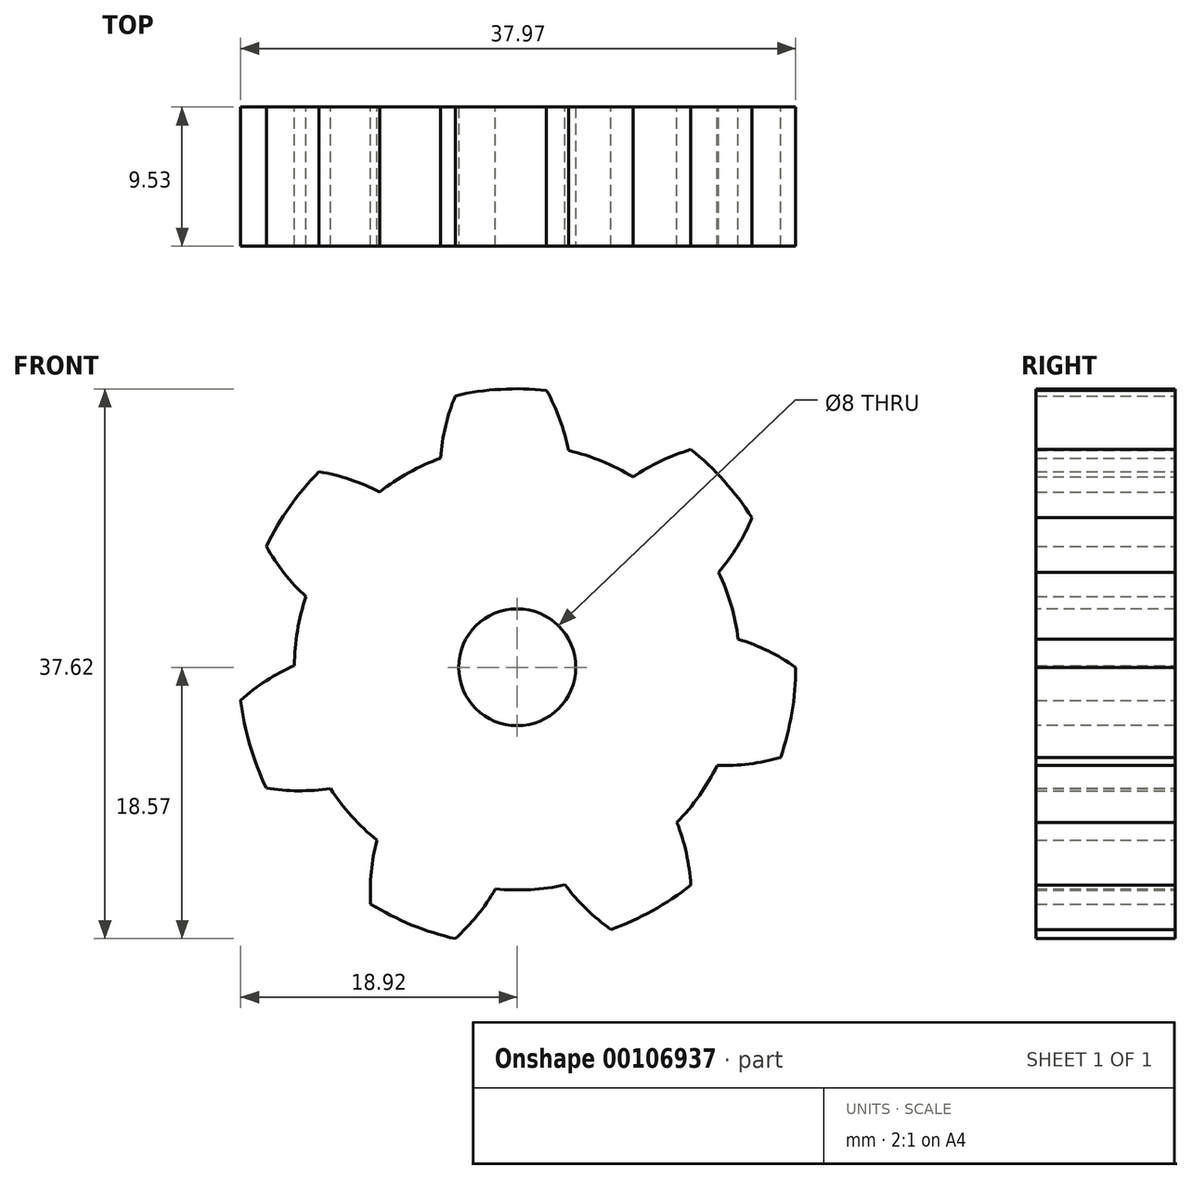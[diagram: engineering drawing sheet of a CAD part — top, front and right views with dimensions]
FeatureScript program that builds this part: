
annotation { "Feature Type Name" : "Feature", "Feature Type Description" : "" }
export const myFeature = defineFeature(function(context is Context, id is Id, definition is map)
    precondition{}
    {
        {
            var Q0;
            Q0=qCreatedBy(makeId("Front.planeOp"),FACE);
            var sketch = newSketch(context, id + "F0", { "sketchPlane" : qUnion([Q0])});
            skCircle(sketch, "E0", {"center": v(0, 0) * mm, "radius": 19.05 * mm, "construction": true});
            skCircle(sketch, "E1", {"center": v(0, 0) * mm, "radius": 15.88 * mm, "construction": true});
            skCircle(sketch, "E2", {"center": v(0, 0) * mm, "radius": 15.24 * mm, "construction": true});
            skLineSegment(sketch, "E3", {"start": v(0, 0) * mm, "end": v(0, 47.47) * mm, "construction": true});
            skLineSegment(sketch, "E4", {"start": v(0, 0) * mm, "end": v(-3.13, 52.63) * mm, "construction": true});
            skLineSegment(sketch, "E5", {"start": v(0, 15.88) * mm, "end": v(-34.16, 15.87) * mm, "construction": true});
            skLineSegment(sketch, "E6", {"start": v(0, 15.88) * mm, "end": v(-34.79, 3.21) * mm, "construction": true});
            skCircle(sketch, "E7", {"center": v(0, 15.88) * mm, "radius": 13.97 * mm, "construction": true});
            skCircle(sketch, "E8", {"center": v(-10.2, 12.16) * mm, "radius": 13.97 * mm, "construction": true});
            skArc(sketch, "E9", {"start": v(3.5, 14.83) * mm, "mid": v(2.92, 16.95) * mm, "end": v(2, 18.94) * mm});
            skArc(sketch, "E10.MirrorCS", {"start": v(-5.24, 14.31) * mm, "mid": v(-4.9, 16.48) * mm, "end": v(-4.24, 18.57) * mm});
            skArc(sketch, "E11", {"start": v(2, 18.94) * mm, "mid": v(-1.13, 19.02) * mm, "end": v(-4.24, 18.57) * mm});
            skArc(sketch, "E12", {"start": v(3.5, 14.83) * mm, "mid": v(-0.9, 15.21) * mm, "end": v(-5.24, 14.31) * mm});
            skSolve(sketch);
        }
        {
            var Q0;
            Q0=makeQuery(id+"F0.imprint","IMPRINT",FACE,{"disambiguationData":[TD([[makeQuery(id+"F0.imprint","IMPRINT",EDGE,{"derivedFrom":sQuery(id+"F0.wireOp",EDGE,"E9")}),1.0]])]});
            extrude(context, id + "F1", {"entities" : qUnion([Q0]), "depth" : 9.52 * mm});
        }
        {
            var Q0;
            Q0=makeQuery(id+"F1.opExtrude","SWEPT_BODY",BODY,{"disambiguationData":[OSD([sQuery(id+"F0.wireOp",EDGE,"E9"),sQuery(id+"F0.wireOp",EDGE,"E10.MirrorCS"),sQuery(id+"F0.wireOp",EDGE,"E11"),sQuery(id+"F0.wireOp",EDGE,"E12")])]});
            var Q1;
            Q1=sQuery(id+"F0.wireOp",EDGE,"E2");
            circularPattern(context, id + "F2", {"entities" : qUnion([Q0]), "axis" : qUnion([Q1]), "angle" : 360 * degree, "instanceCount" : 7, "equalSpace" : true});
        }
        {
            var Q0;
            Q0=qCreatedBy(makeId("Front.planeOp"),FACE);
            var sketch = newSketch(context, id + "F3", { "sketchPlane" : qUnion([Q0])});
            skCircle(sketch, "E13.0", {"center": v(0, 0) * mm, "radius": 15.24 * mm});
            skSolve(sketch);
        }
        {
            var Q0;
            Q0=makeQuery(id+"F3.imprint","IMPRINT",FACE,{"disambiguationData":[TD([[makeQuery(id+"F3.imprint","IMPRINT",EDGE,{"derivedFrom":sQuery(id+"F3.wireOp",EDGE,"E13.0")}),1.0]])]});
            var Q1;
            Q1=makeQuery(id+"F1.opExtrude","CAP_FACE",FACE,{"disambiguationData":[OSD([sQuery(id+"F0.wireOp",EDGE,"E9"),sQuery(id+"F0.wireOp",EDGE,"E10.MirrorCS"),sQuery(id+"F0.wireOp",EDGE,"E11"),sQuery(id+"F0.wireOp",EDGE,"E12")])],"isStart":false});
            extrude(context, id + "F4", {"entities" : qUnion([Q0]), "operationType" : NewBodyOperationType.ADD, "endBound" : BoundingType.UP_TO_SURFACE, "endBoundEntityFace" : qUnion([Q1]), "depth" : 25.4 * mm});
        }
        {
            var Q0;
            {var subQ0=sQuery(id+"F0.wireOp",EDGE,"E12");var subQ1=sQuery(id+"F0.wireOp",EDGE,"E11");var subQ2=sQuery(id+"F0.wireOp",EDGE,"E10.MirrorCS");var subQ3=sQuery(id+"F0.wireOp",EDGE,"E9");var subQ4=makeQuery(id+"F1.opExtrude","CAP_FACE",FACE,{"disambiguationData":[OSD([subQ3,subQ2,subQ1,subQ0])],"isStart":false});Q0=makeQuery(id+"F4.boolean.opBoolean","MERGE",FACE,{"derivedFrom":[subQ4,makeQuery(id+"F2.opPattern","COPY",FACE,{"derivedFrom":subQ4,"instanceName":"1"}),makeQuery(id+"F2.opPattern","COPY",FACE,{"derivedFrom":subQ4,"instanceName":"2"}),makeQuery(id+"F2.opPattern","COPY",FACE,{"derivedFrom":subQ4,"instanceName":"3"}),makeQuery(id+"F2.opPattern","COPY",FACE,{"derivedFrom":subQ4,"instanceName":"4"}),makeQuery(id+"F2.opPattern","COPY",FACE,{"derivedFrom":subQ4,"instanceName":"5"}),makeQuery(id+"F2.opPattern","COPY",FACE,{"derivedFrom":subQ4,"instanceName":"6"}),makeQuery(id+"F4.opExtrude","CAP_FACE",FACE,{"disambiguationData":[OSD([subQ3,subQ2,subQ1,subQ0])],"isStart":false})]});}
            var sketch = newSketch(context, id + "F5", { "sketchPlane" : qUnion([Q0])});
            skCircle(sketch, "E14", {"center": v(0, 0) * mm, "radius": 4 * mm});
            skSolve(sketch);
        }
        {
            var Q0;
            Q0 = qSketchRegion(id + "F5", true);
            extrude(context, id + "F6", {"entities" : qUnion([Q0]), "operationType" : NewBodyOperationType.REMOVE, "endBound" : BoundingType.THROUGH_ALL, "oppositeDirection" : true, "depth" : 25.4 * mm});
        }
    });
